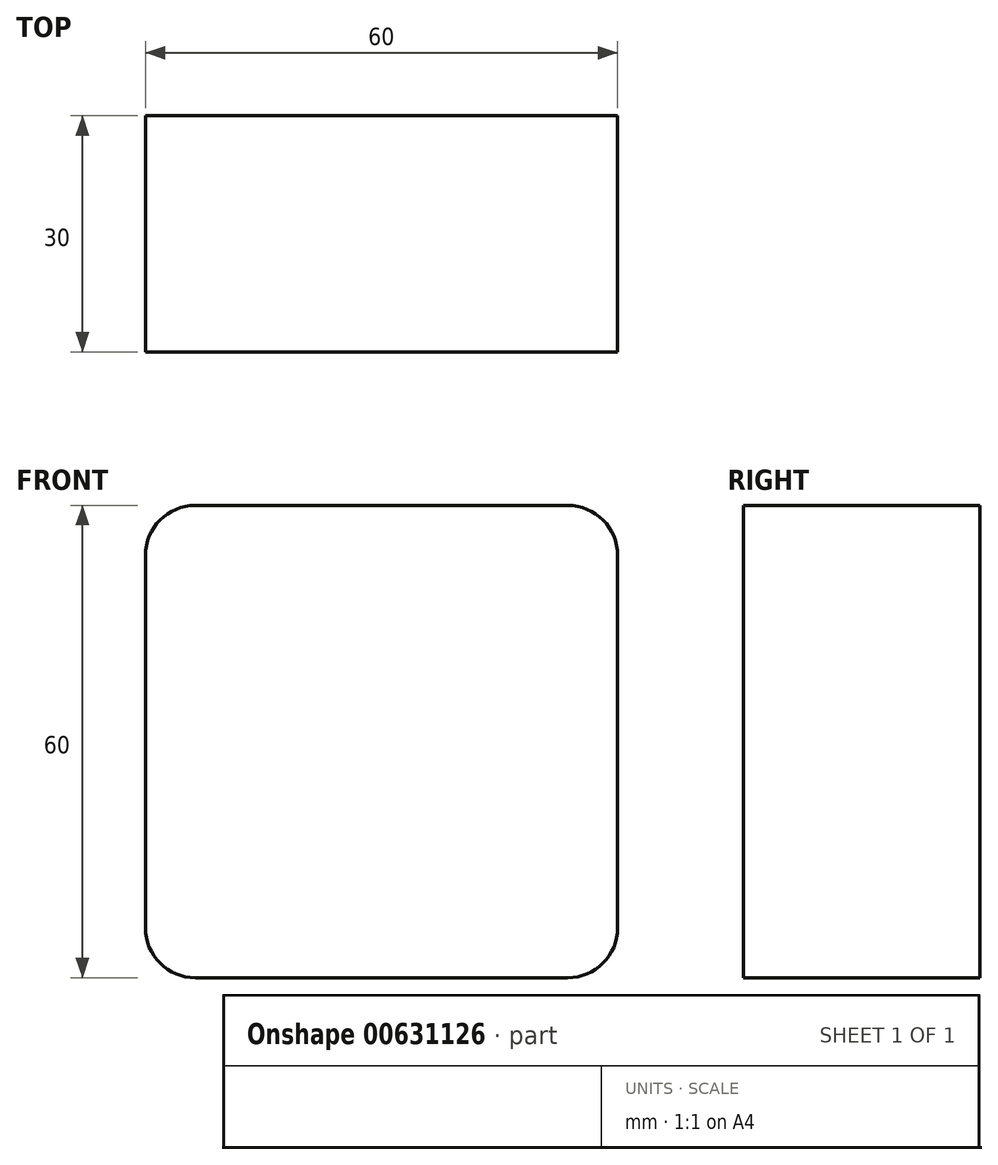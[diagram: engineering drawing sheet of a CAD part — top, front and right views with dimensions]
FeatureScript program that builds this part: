
annotation { "Feature Type Name" : "Feature", "Feature Type Description" : "" }
export const myFeature = defineFeature(function(context is Context, id is Id, definition is map)
    precondition{}
    {
        {
            var Q0;
            Q0=qCreatedBy(makeId("Front.planeOp"),FACE);
            var sketch = newSketch(context, id + "F0", { "sketchPlane" : qUnion([Q0])});
            skLineSegment(sketch, "E0.bottom", {"start": v(6.35, 41.8) * mm, "end": v(53.65, 41.8) * mm});
            skLineSegment(sketch, "E0.top", {"start": v(6.35, -18.2) * mm, "end": v(53.65, -18.2) * mm});
            skLineSegment(sketch, "E0.left", {"start": v(0, 35.44) * mm, "end": v(0, -11.86) * mm});
            skLineSegment(sketch, "E0.right", {"start": v(60, 35.44) * mm, "end": v(60, -11.86) * mm});
            skPoint(sketch, "E1.visualSharp", {"position": v(0, 41.8) * mm});
            skArc(sketch, "E1.filletArc", {"start": v(6.35, 41.8) * mm, "mid": v(1.86, 39.94) * mm, "end": v(0, 35.44) * mm});
            skPoint(sketch, "E2.visualSharp", {"position": v(60, 41.8) * mm});
            skArc(sketch, "E2.filletArc", {"start": v(60, 35.44) * mm, "mid": v(58.14, 39.94) * mm, "end": v(53.65, 41.8) * mm});
            skPoint(sketch, "E3.visualSharp", {"position": v(0, -18.2) * mm});
            skArc(sketch, "E3.filletArc", {"start": v(0, -11.86) * mm, "mid": v(1.86, -16.35) * mm, "end": v(6.35, -18.2) * mm});
            skPoint(sketch, "E4.visualSharp", {"position": v(60, -18.2) * mm});
            skArc(sketch, "E4.filletArc", {"start": v(53.65, -18.2) * mm, "mid": v(58.14, -16.35) * mm, "end": v(60, -11.86) * mm});
            skSolve(sketch);
        }
        {
            var Q0;
            Q0 = qSketchRegion(id + "F0", true);
            extrude(context, id + "F1", {"entities" : qUnion([Q0]), "oppositeDirection" : true, "depth" : 30 * mm, "offsetDistance" : 25 * mm});
        }
    });
